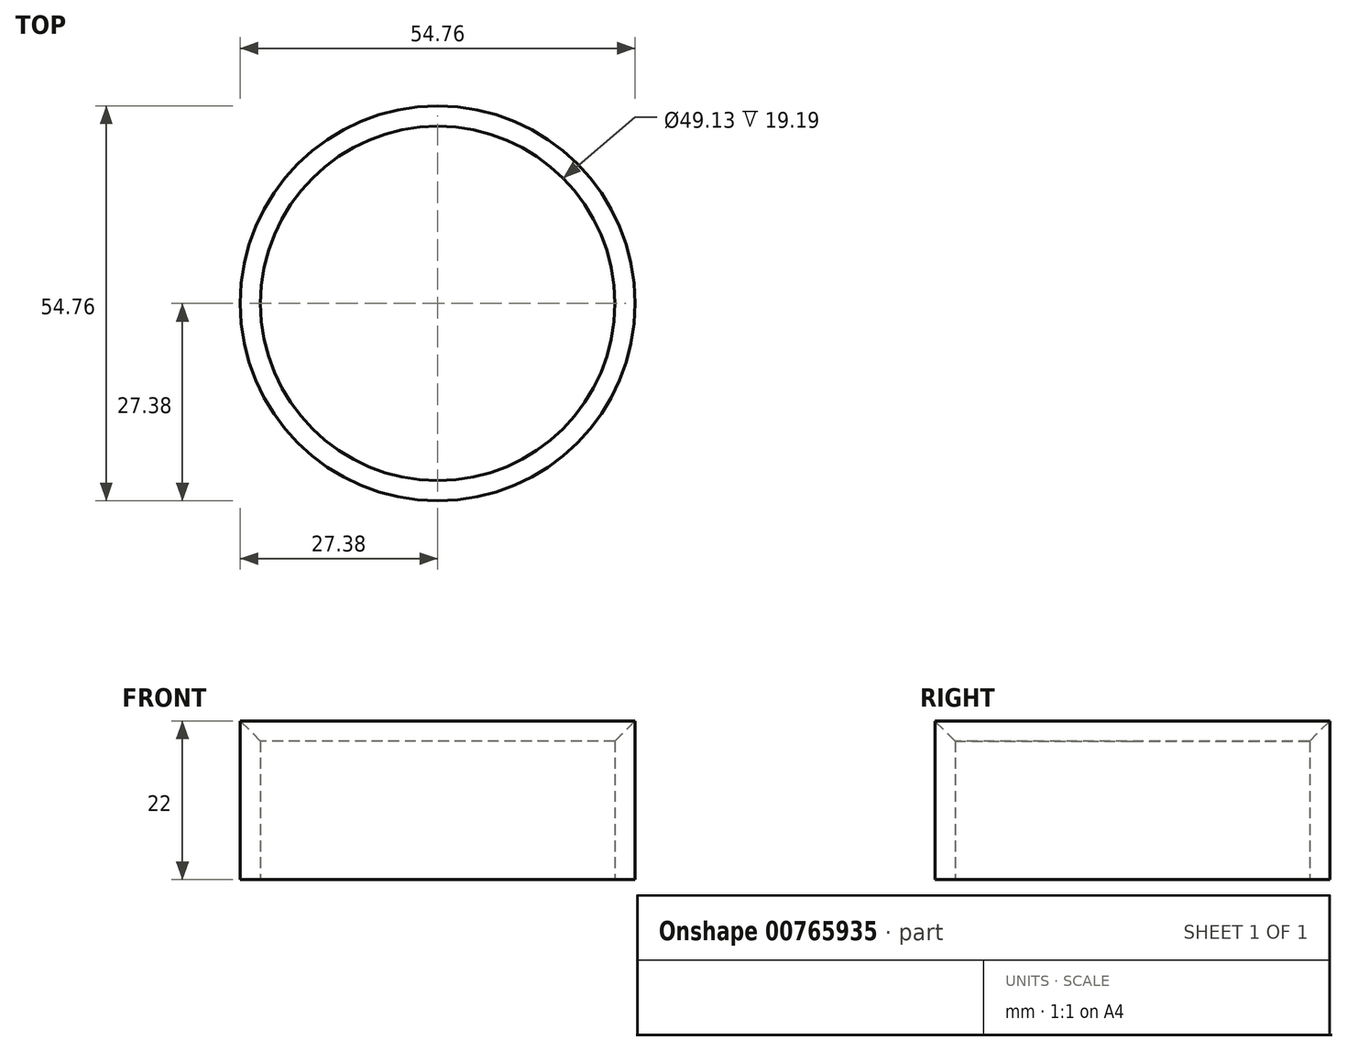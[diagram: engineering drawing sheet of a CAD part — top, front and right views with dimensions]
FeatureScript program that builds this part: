
annotation { "Feature Type Name" : "Feature", "Feature Type Description" : "" }
export const myFeature = defineFeature(function(context is Context, id is Id, definition is map)
    precondition{}
    {
        {
            var Q0;
            Q0=qCreatedBy(makeId("Top.planeOp"),FACE);
            var sketch = newSketch(context, id + "F0", { "sketchPlane" : qUnion([Q0])});
            skCircle(sketch, "E0", {"center": v(0, 0) * mm, "radius": 24.57 * mm});
            skCircle(sketch, "E1", {"center": v(0, 0) * mm, "radius": 27.38 * mm});
            skSolve(sketch);
        }
        {
            var Q0;
            Q0=makeQuery(id+"F0.imprint","IMPRINT",FACE,{"disambiguationData":[TD([[makeQuery(id+"F0.imprint","IMPRINT",EDGE,{"derivedFrom":sQuery(id+"F0.wireOp",EDGE,"E0")}),-1.0]])]});
            extrude(context, id + "F1", {"entities" : qUnion([Q0]), "depth" : 22.09 * mm, "offsetDistance" : 25 * mm});
        }
        {
            var Q0;
            Q0=makeQuery(id+"F1.opExtrude","CAP_EDGE",EDGE,{"disambiguationData":[OSD([sQuery(id+"F0.wireOp",EDGE,"E0")])],"isStart":false});
            chamfer(context, id + "F2", {"entities" : qUnion([Q0]), "chamferType" : ChamferType.OFFSET_ANGLE, "width" : 2.9 * mm, "oppositeDirection" : false, "angle" : 45 * degree, "tangentPropagation" : true});
        }
    });
